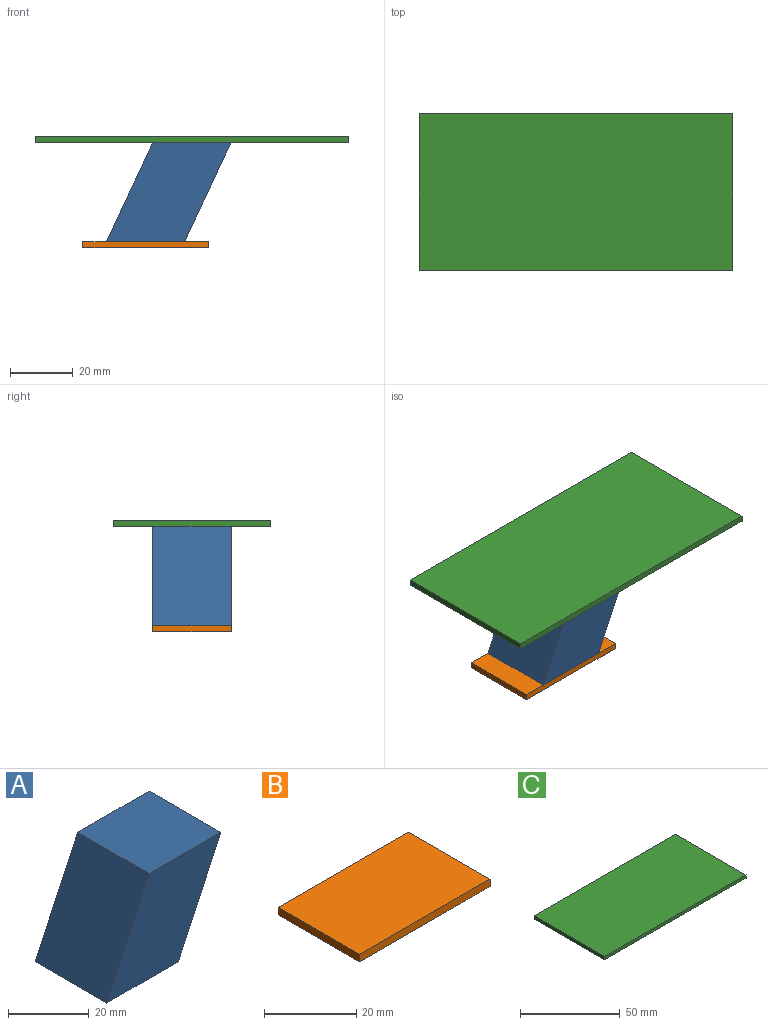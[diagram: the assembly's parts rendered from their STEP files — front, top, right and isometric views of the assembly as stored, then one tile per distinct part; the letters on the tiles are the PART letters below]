
ASSEMBLY  parts=3 mates=2
PART A: 6 faces, bbox 39.8x25x31.7 mm
  f0: plane 25x25mm, normal (0,0,-1), area 625mm2, adj f1,f3,f4,f5
  f1: plane 31.7x25mm, normal (0.91,0,-0.42), area 875mm2, adj f0,f2,f4,f5
  f2: plane 25x25mm, normal (0,0,1), area 625mm2, adj f1,f3,f4,f5
  f3: plane 31.7x25mm, normal (-0.91,0,0.42), area 875mm2, adj f0,f2,f4,f5
  f4: plane 39.83x31.7mm, normal (0,-1,0), area 792.6mm2, adj f0,f1,f2,f3
  f5: plane 39.83x31.7mm, normal (0,1,0), area 792.6mm2, adj f0,f1,f2,f3
PART B: 6 faces, bbox 40x25x2 mm
  f0: plane 25x2mm, normal (1,0,0), area 50mm2, adj f1,f3,f4,f5
  f1: plane 40x2mm, normal (0,1,0), area 80mm2, adj f0,f2,f4,f5
  f2: plane 25x2mm, normal (-1,0,0), area 50mm2, adj f1,f3,f4,f5
  f3: plane 40x2mm, normal (0,-1,0), area 80mm2, adj f0,f2,f4,f5
  f4: plane 40x25mm, normal (0,0,1), area 1000mm2, adj f0,f1,f2,f3
  f5: plane 40x25mm, normal (0,0,-1), area 1000mm2, adj f0,f1,f2,f3
PART C: 6 faces, bbox 100x50x2 mm
  f0: plane 50x2mm, normal (1,0,0), area 100mm2, adj f1,f3,f4,f5
  f1: plane 100x2mm, normal (0,1,0), area 200mm2, adj f0,f2,f4,f5
  f2: plane 50x2mm, normal (-1,0,0), area 100mm2, adj f1,f3,f4,f5
  f3: plane 100x2mm, normal (0,-1,0), area 200mm2, adj f0,f2,f4,f5
  f4: plane 100x50mm, normal (0,0,1), area 5000mm2, adj f0,f1,f2,f3
  f5: plane 100x50mm, normal (0,0,-1), area 5000mm2, adj f0,f1,f2,f3
PLACE A t=(-27.71,28.31,45.11)mm
PLACE B t=(-32.52,3.31,5.05)mm fixed
PLACE C t=(12.31,-9.19,38.75)mm
MATE fastened A.f0 <-> B.f4  axis (0,0,-1) through (-52.52,15.81,7.05)mm
MATE fastened C.f5 <-> A.f2  axis (0,0,-1) through (-37.69,15.81,38.75)mm
